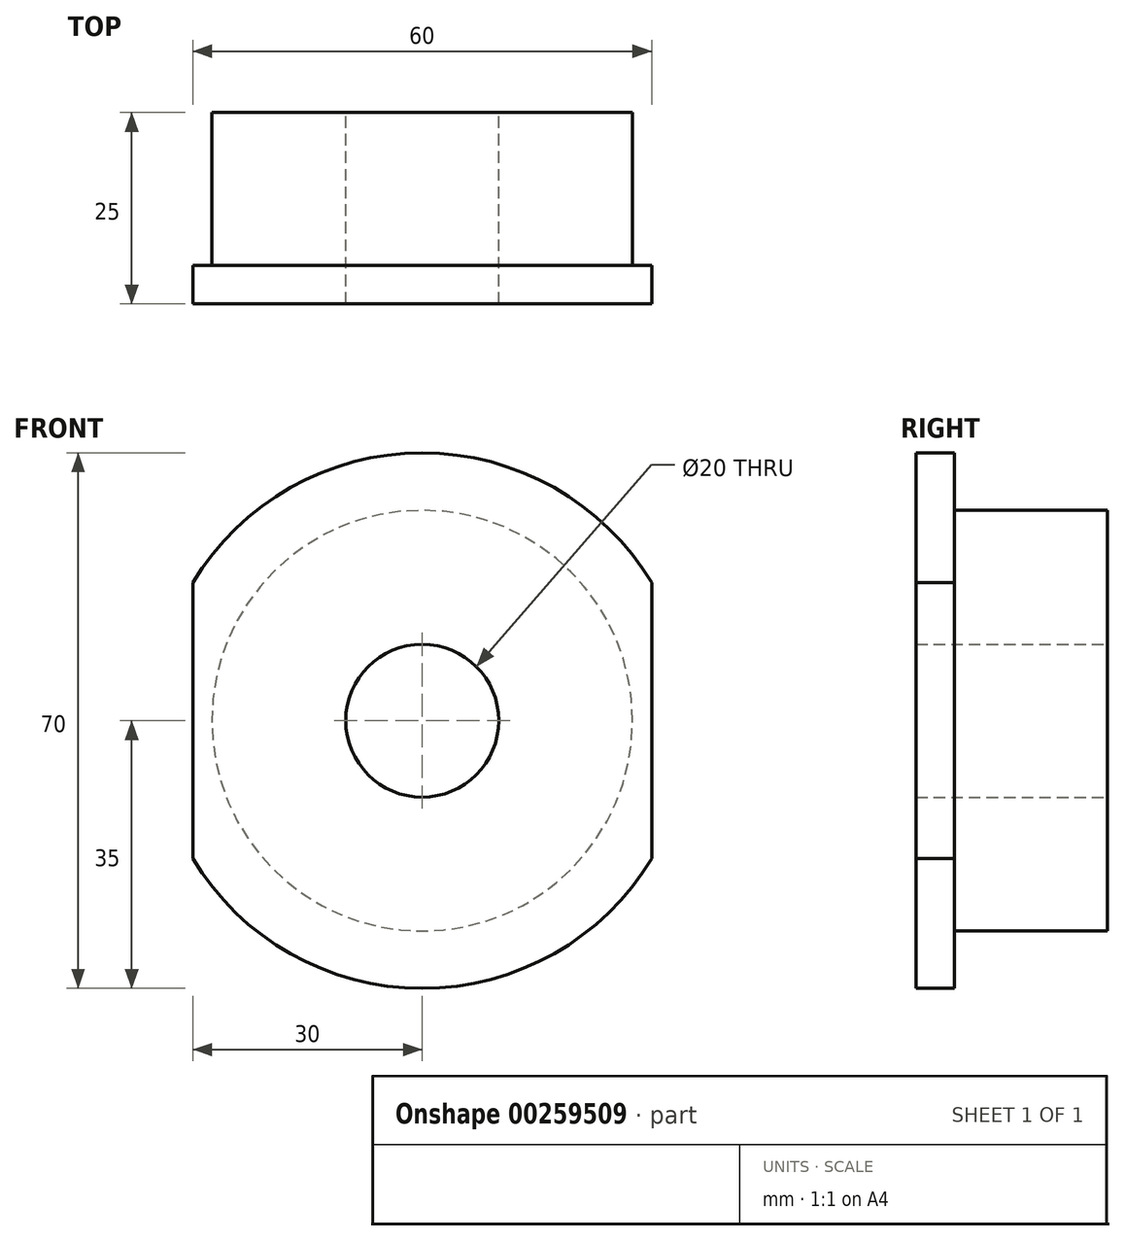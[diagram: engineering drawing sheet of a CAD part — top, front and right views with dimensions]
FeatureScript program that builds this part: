
annotation { "Feature Type Name" : "Feature", "Feature Type Description" : "" }
export const myFeature = defineFeature(function(context is Context, id is Id, definition is map)
    precondition{}
    {
        {
            var Q0;
            Q0=qCreatedBy(makeId("Front.planeOp"),FACE);
            var sketch = newSketch(context, id + "F0", { "sketchPlane" : qUnion([Q0])});
            skCircle(sketch, "E0", {"center": v(0, 0) * mm, "radius": 35 * mm});
            skCircle(sketch, "E1", {"center": v(0, 0) * mm, "radius": 10 * mm});
            skSolve(sketch);
        }
        {
            var Q0;
            Q0 = qSketchRegion(id + "F0", true);
            extrude(context, id + "F1", {"entities" : qUnion([Q0]), "depth" : 25 * mm});
        }
        {
            var Q0;
            Q0=makeQuery(id+"F1.opExtrude","CAP_FACE",FACE,{"disambiguationData":[OSD([sQuery(id+"F0.wireOp",EDGE,"E0"),sQuery(id+"F0.wireOp",EDGE,"E1")])],"isStart":true});
            var sketch = newSketch(context, id + "F2", { "sketchPlane" : qUnion([Q0])});
            skCircle(sketch, "E2", {"center": v(0, 0) * mm, "radius": 27.5 * mm});
            skCircle(sketch, "E3", {"center": v(0, 0) * mm, "radius": 35 * mm});
            skSolve(sketch);
        }
        {
            var Q0;
            Q0 = qSketchRegion(id + "F2", true);
            extrude(context, id + "F3", {"entities" : qUnion([Q0]), "operationType" : NewBodyOperationType.REMOVE, "oppositeDirection" : true, "depth" : 20 * mm});
        }
        {
            var Q0;
            Q0=makeQuery(id+"F1.opExtrude","CAP_FACE",FACE,{"disambiguationData":[OSD([sQuery(id+"F0.wireOp",EDGE,"E0"),sQuery(id+"F0.wireOp",EDGE,"E1")])],"isStart":false});
            var sketch = newSketch(context, id + "F4", { "sketchPlane" : qUnion([Q0])});
            skLineSegment(sketch, "E4.bottom", {"start": v(-30, 29.37) * mm, "end": v(-43.36, 29.37) * mm});
            skLineSegment(sketch, "E4.top", {"start": v(-30, -33.2) * mm, "end": v(-43.36, -33.2) * mm});
            skLineSegment(sketch, "E4.left", {"start": v(-30, 29.37) * mm, "end": v(-30, -33.2) * mm});
            skLineSegment(sketch, "E4.right", {"start": v(-43.36, 29.37) * mm, "end": v(-43.36, -33.2) * mm});
            skLineSegment(sketch, "E5.MirrorCS", {"start": v(30, 29.37) * mm, "end": v(43.36, 29.37) * mm});
            skLineSegment(sketch, "E6.MirrorCS", {"start": v(43.36, 29.37) * mm, "end": v(43.36, -33.2) * mm});
            skLineSegment(sketch, "E7.MirrorCS", {"start": v(30, 29.37) * mm, "end": v(30, -33.2) * mm});
            skLineSegment(sketch, "E8.MirrorCS", {"start": v(30, -33.2) * mm, "end": v(43.36, -33.2) * mm});
            skSolve(sketch);
        }
        {
            var Q0;
            Q0 = qSketchRegion(id + "F4", true);
            extrude(context, id + "F5", {"entities" : qUnion([Q0]), "operationType" : NewBodyOperationType.REMOVE, "oppositeDirection" : true, "depth" : 25 * mm});
        }
    });
